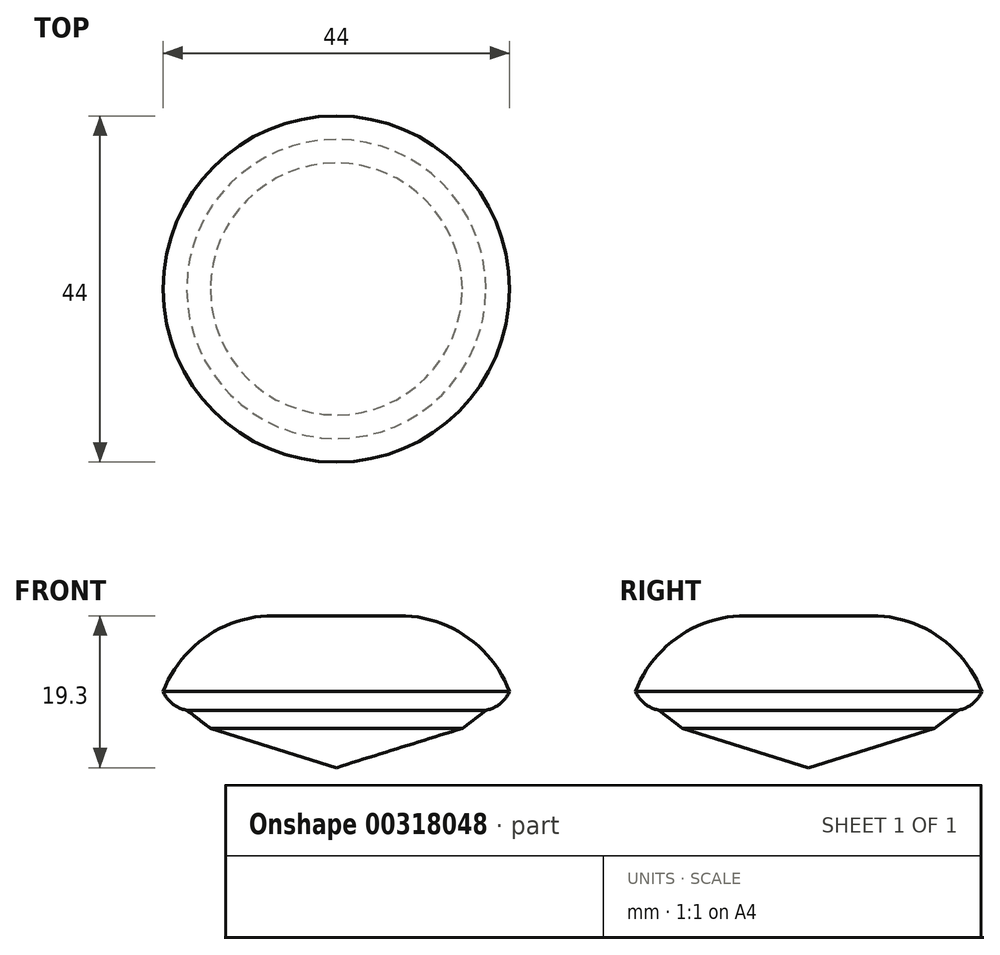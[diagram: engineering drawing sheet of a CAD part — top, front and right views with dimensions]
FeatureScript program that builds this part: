
annotation { "Feature Type Name" : "Feature", "Feature Type Description" : "" }
export const myFeature = defineFeature(function(context is Context, id is Id, definition is map)
    precondition{}
    {
        {
            var Q0;
            Q0=qCreatedBy(makeId("Front.planeOp"),FACE);
            var sketch = newSketch(context, id + "F0", { "sketchPlane" : qUnion([Q0])});
            skLineSegment(sketch, "E0", {"start": v(0, 0) * mm, "end": v(8, 0) * mm});
            skArc(sketch, "E1", {"start": v(22, -9.61) * mm, "mid": v(16.5, -2.64) * mm, "end": v(8, 0) * mm});
            skArc(sketch, "E2", {"start": v(19, -12) * mm, "mid": v(20.8, -11.2) * mm, "end": v(22, -9.61) * mm});
            skLineSegment(sketch, "E3", {"start": v(19, -12) * mm, "end": v(0, -12) * mm});
            skLineSegment(sketch, "E4", {"start": v(16, -14.3) * mm, "end": v(0, -14.3) * mm});
            skLineSegment(sketch, "E5", {"start": v(19, -12) * mm, "end": v(16, -14.3) * mm});
            skLineSegment(sketch, "E6", {"start": v(16, -14.3) * mm, "end": v(0, -19.3) * mm});
            skLineSegment(sketch, "E7", {"start": v(0, -19.3) * mm, "end": v(0, 0) * mm});
            skSolve(sketch);
        }
        {
            var Q0;
            {var subQ0=sQuery(id+"F0.wireOp",EDGE,"E4");Q0=makeQuery(id+"F0.imprint","IMPRINT",FACE,{"disambiguationData":[TD([[makeQuery(id+"F0.imprint","IMPRINT",EDGE,{"derivedFrom":subQ0}),1.0]])]});}
            var Q1;
            {var subQ0=sQuery(id+"F0.wireOp",EDGE,"E3");Q1=makeQuery(id+"F0.imprint","IMPRINT",FACE,{"disambiguationData":[TD([[makeQuery(id+"F0.imprint","IMPRINT",EDGE,{"derivedFrom":subQ0}),1.0]])]});}
            var Q2;
            {var subQ1=sQuery(id+"F0.wireOp",EDGE,"E0");Q2=makeQuery(id+"F0.imprint","IMPRINT",FACE,{"disambiguationData":[TD([[makeQuery(id+"F0.imprint","IMPRINT",EDGE,{"derivedFrom":subQ1}),-1.0]])]});}
            var Q3;
            Q3=sQuery(id+"F0.wireOp",EDGE,"E7");
            revolve(context, id + "F1", {"entities" : qUnion([Q0, Q1, Q2]), "axis" : qUnion([Q3]), "revolveType" : RevolveType.FULL});
        }
    });
